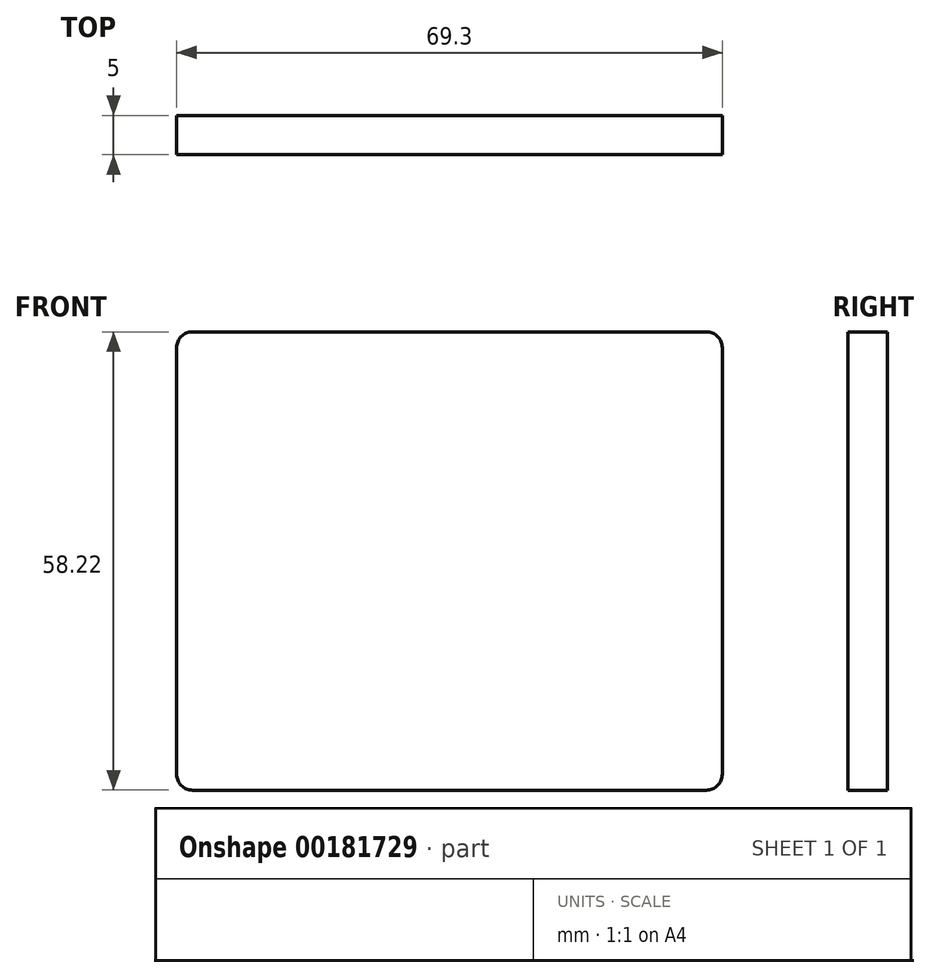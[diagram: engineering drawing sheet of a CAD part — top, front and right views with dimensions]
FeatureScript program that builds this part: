
annotation { "Feature Type Name" : "Feature", "Feature Type Description" : "" }
export const myFeature = defineFeature(function(context is Context, id is Id, definition is map)
    precondition{}
    {
        {
            var Q0;
            Q0=qCreatedBy(makeId("Front.planeOp"),FACE);
            var sketch = newSketch(context, id + "F0", { "sketchPlane" : qUnion([Q0])});
            skLineSegment(sketch, "E0.bottom", {"start": v(-34.65, 29.11) * mm, "end": v(34.65, 29.11) * mm});
            skLineSegment(sketch, "E0.top", {"start": v(-34.65, -29.11) * mm, "end": v(34.65, -29.11) * mm});
            skLineSegment(sketch, "E0.left", {"start": v(-34.65, 29.11) * mm, "end": v(-34.65, -29.11) * mm});
            skLineSegment(sketch, "E0.right", {"start": v(34.65, 29.11) * mm, "end": v(34.65, -29.11) * mm});
            skPoint(sketch, "E0.middle", {"position": v(0, 0) * mm});
            skSolve(sketch);
        }
        {
            var Q0;
            Q0 = qSketchRegion(id + "F0", true);
            extrude(context, id + "F1", {"entities" : qUnion([Q0]), "depth" : 5 * mm});
        }
        {
            var Q0;
            Q0=makeQuery(id+"F1.opExtrude","CAP_FACE",FACE,{"disambiguationData":[OSD([sQuery(id+"F0.wireOp",EDGE,"E0.bottom"),sQuery(id+"F0.wireOp",EDGE,"E0.top"),sQuery(id+"F0.wireOp",EDGE,"E0.left"),sQuery(id+"F0.wireOp",EDGE,"E0.right")])],"isStart":false});
            var sketch = newSketch(context, id + "F2", { "sketchPlane" : qUnion([Q0])});
            skText(sketch, "E1", { "text": "made in usa\n", "fontName": "OpenSans-Bold.ttf"});
            const initialGuessF2  = {"E1": [-0.01723, 0.0154, 1, 0, 0.00417]};
            skSetInitialGuess(sketch, initialGuessF2);
            skSolve(sketch);
        }
        {
            var Q0;
            Q0=makeQuery(id+"F1.opExtrude","SWEPT_EDGE",EDGE,{"disambiguationData":[OSD([sQuery(id+"F0.wireOp",EDGE,"E0.bottom"),sQuery(id+"F0.wireOp",EDGE,"E0.right")])]});
            var Q1;
            Q1=makeQuery(id+"F1.opExtrude","SWEPT_EDGE",EDGE,{"disambiguationData":[OSD([sQuery(id+"F0.wireOp",EDGE,"E0.bottom"),sQuery(id+"F0.wireOp",EDGE,"E0.left")])]});
            var Q2;
            Q2=makeQuery(id+"F1.opExtrude","SWEPT_EDGE",EDGE,{"disambiguationData":[OSD([sQuery(id+"F0.wireOp",EDGE,"E0.top"),sQuery(id+"F0.wireOp",EDGE,"E0.right")])]});
            var Q3;
            Q3=makeQuery(id+"F1.opExtrude","SWEPT_EDGE",EDGE,{"disambiguationData":[OSD([sQuery(id+"F0.wireOp",EDGE,"E0.top"),sQuery(id+"F0.wireOp",EDGE,"E0.left")])]});
            fillet(context, id + "F3", {"entities" : qUnion([Q0, Q1, Q2, Q3]), "radius" : 2 * mm, "tangentPropagation" : true, "allowEdgeOverflow" : false});
        }
    });
